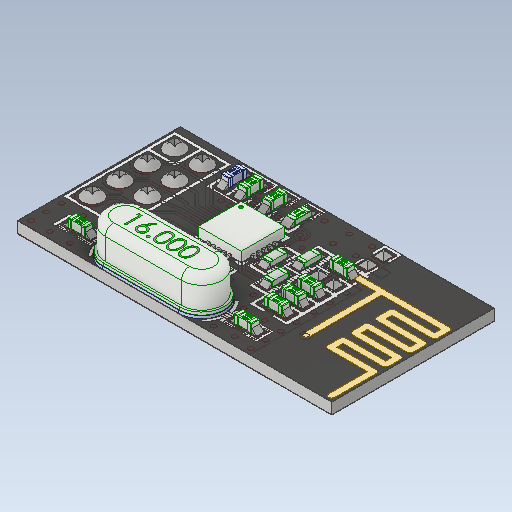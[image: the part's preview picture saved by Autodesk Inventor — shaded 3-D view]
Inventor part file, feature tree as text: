
AUTODESK INVENTOR PART (.ipt)
format: ipt  version: 2020.1 (Build 241239000, 239)  size: 6,878,208 bytes
history: mixed  units: mm
features: other x99, loft x29, boolean_combine x2, imported_body x1
ambient origin geometry x8: Origin, YZ Plane, XZ Plane, XY Plane, X Axis, Y Axis, Z Axis, Center Point
bodies: Solid1 (imported_parasolid), Solid2 (imported_parasolid), Solid3 (imported_parasolid), Solid4 (imported_parasolid), Solid5 (imported_parasolid), Solid6 (imported_parasolid), Solid7 (imported_parasolid), Solid8 (imported_parasolid), Solid9 (imported_parasolid), Solid10 (imported_parasolid), Solid11 (imported_parasolid), Solid12 (imported_parasolid), Solid13 (imported_parasolid), Solid14 (imported_parasolid), Solid15 (imported_parasolid), Solid16 (imported_parasolid), Solid17 (imported_parasolid), Solid18 (imported_parasolid), Solid19 (imported_parasolid), Solid20 (imported_parasolid), Solid21 (imported_parasolid), Solid22 (imported_parasolid), Solid23 (imported_parasolid), Solid24 (imported_parasolid), Solid25 (imported_parasolid), Solid26 (imported_parasolid), Solid27 (imported_parasolid), Solid28 (imported_parasolid), Solid29 (imported_parasolid), Solid30 (imported_parasolid), Solid31 (imported_parasolid), Solid32 (imported_parasolid), Solid33 (imported_parasolid), Solid34 (imported_parasolid), Solid35 (imported_parasolid), Solid36 (imported_parasolid), Solid37 (imported_parasolid), Solid38 (imported_parasolid), Solid39 (imported_parasolid), Solid40 (imported_parasolid), Solid41 (imported_parasolid), Solid42 (imported_parasolid), Solid43 (imported_parasolid), Solid44 (imported_parasolid), Solid45 (imported_parasolid), Solid46 (imported_parasolid), Solid47 (imported_parasolid), Solid48 (imported_parasolid), Solid49 (imported_parasolid), Solid50 (imported_parasolid), Solid51 (imported_parasolid), Solid52 (imported_parasolid), Solid53 (imported_parasolid), Solid54 (imported_parasolid), Solid55 (imported_parasolid), Solid56 (imported_parasolid), Solid57 (imported_parasolid), Solid58 (imported_parasolid), Solid59 (imported_parasolid), Solid60 (imported_parasolid), Solid61 (imported_parasolid), Solid62 (imported_parasolid), Solid63 (imported_parasolid), Solid64 (imported_parasolid), Solid65 (imported_parasolid), Solid66 (imported_parasolid), Solid67 (imported_parasolid), Solid68 (imported_parasolid), Solid69 (imported_parasolid), Solid70 (imported_parasolid), Solid71 (imported_parasolid), Solid72 (imported_parasolid), Solid73 (imported_parasolid), Solid74 (imported_parasolid), Solid75 (imported_parasolid), Solid76 (imported_parasolid), Solid77 (imported_parasolid), Solid78 (imported_parasolid), Solid79 (imported_parasolid), Solid80 (imported_parasolid), Solid81 (imported_parasolid), Solid82 (imported_parasolid), Solid83 (imported_parasolid), Solid84 (imported_parasolid), Solid85 (imported_parasolid), Solid86 (imported_parasolid), Solid87 (imported_parasolid), Solid88 (imported_parasolid), Solid89 (imported_parasolid), Solid90 (imported_parasolid), Solid91 (imported_parasolid), Solid92 (imported_parasolid), Solid93 (imported_parasolid), Solid94 (imported_parasolid), Solid95 (imported_parasolid), Solid96 (imported_parasolid), Solid97 (imported_parasolid), Solid98 (imported_parasolid), Solid99 (imported_parasolid), Solid100 (imported_parasolid), Solid101 (imported_parasolid), Solid102 (imported_parasolid), Solid103 (imported_parasolid), Solid104 (imported_parasolid), Solid105 (imported_parasolid), Solid106 (imported_parasolid), Solid107 (imported_parasolid), Solid108 (imported_parasolid), Solid109 (imported_parasolid), Solid110 (imported_parasolid), Solid111 (imported_parasolid), Solid112 (imported_parasolid), Solid113 (imported_parasolid), Solid114 (imported_parasolid), Solid115 (imported_parasolid), Solid116 (imported_parasolid), Solid117 (imported_parasolid), Solid118 (imported_parasolid), Solid119 (imported_parasolid), Solid120 (imported_parasolid), Solid121 (imported_parasolid), Solid122 (imported_parasolid), Solid123 (imported_parasolid), Solid124 (imported_parasolid), Solid125 (imported_parasolid), Solid126 (imported_parasolid), Solid127 (imported_parasolid), Solid128 (imported_parasolid), Solid129 (imported_parasolid), Solid130 (imported_parasolid)
feature tree (131):
  other  "PCB Body"
  other  "Cut-Extrude1[2]"
  other  "Cut-Extrude1[3]"
  other  "Cut-Extrude1[4]"
  other  "Cut-Extrude1[5]"
  other  "Cut-Extrude1[6]"
  other  "Cut-Extrude1[7]"
  other  "Cut-Extrude1[8]"
  other  "Cut-Extrude1[9]"
  other  "Cut-Extrude1[10]"
  other  "Cut-Extrude1[11]"
  other  "Cut-Extrude1[12]"
  other  "Cut-Extrude1[13]"
  other  "Cut-Extrude2[1]"
  other  "Cut-Extrude2[2]"
  other  "Cut-Extrude2[3]"
  other  "Cut-Extrude2[4]"
  other  "_Capacitor 1608_-_Solid7_"
  other  "Body-Move_Copy21"
  other  "Body-Move_Copy22"
  other  "_Resistor 1608_-_Imported1_"
  other  "Body-Move_Copy26"
  other  "Body-Move_Copy28"
  other  "Body-Move_Copy29[1]"
  other  "Body-Move_Copy29[2]"
  other  "Body-Move_Copy30"
  other  "Body-Move_Copy31"
  other  "Body-Move_Copy34"
  other  "_rg1608p-103-b_-_rg1608p-103-b_"
  other  "Body-Move_Copy38"
  other  "Body-Move_Copy39"
  other  "_QFN-20 with Pad_-_Вытянуть4_"
  other  "Boss-Extrude22"
  other  "Boss-Extrude28"
  other  "Body-Move_Copy50"
  other  "Boss-Extrude31"
  other  "Cut-Extrude3"
  loft  "Loft2"
  loft  "Loft4"
  loft  "Loft7"
  loft  "Loft9"
  loft  "Loft10"
  loft  "Loft12"
  loft  "Loft13"
  loft  "Loft14"
  loft  "Loft15"
  loft  "Loft16"
  loft  "Loft17"
  loft  "Loft18"
  loft  "Loft19"
  loft  "Loft20"
  loft  "Loft21"
  loft  "Loft22"
  loft  "Loft23"
  loft  "Loft24"
  loft  "Loft25"
  loft  "Loft26"
  loft  "Loft27"
  loft  "Loft28"
  loft  "Loft29"
  loft  "Loft30"
  loft  "Loft31"
  loft  "Loft32"
  loft  "Loft33"
  loft  "Loft34"
  loft  "Loft35"
  other  "Body-Move_Copy51[1]"
  other  "Body-Move_Copy51[2]"
  other  "Body-Move_Copy51[3]"
  other  "Body-Move_Copy51[4]"
  other  "Body-Move_Copy53[1]"
  other  "Body-Move_Copy53[2]"
  other  "Body-Move_Copy53[3]"
  other  "Body-Move_Copy53[4]"
  other  "Body-Move_Copy53[5]"
  other  "Body-Move_Copy57[1]"
  other  "Body-Move_Copy57[2]"
  other  "Body-Move_Copy57[3]"
  other  "Body-Move_Copy57[4]"
  other  "Body-Move_Copy57[5]"
  other  "Body-Move_Copy57[6]"
  other  "Body-Move_Copy57[7]"
  other  "Body-Move_Copy57[8]"
  other  "Body-Move_Copy57[9]"
  other  "Body-Move_Copy57[10]"
  other  "Boss-Extrude38[1]"
  other  "Boss-Extrude38[2]"
  other  "Boss-Extrude38[3]"
  other  "Boss-Extrude38[4]"
  other  "Cut-Extrude4[1]"
  other  "Cut-Extrude4[2]"
  other  "_Header 2_54 Vertical 1x2_-_Chamfer2_"
  other  "Cut-Extrude5[1]"
  other  "Cut-Extrude5[2]"
  other  "Cut-Extrude5[3]"
  other  "Cut-Extrude5[4]"
  other  "Cut-Extrude5[5]"
  other  "Cut-Extrude5[6]"
  other  "Cut-Extrude5[7]"
  other  "Cut-Extrude5[8]"
  other  "Boss-Extrude43"
  other  "Boss-Extrude45[1]"
  other  "Boss-Extrude45[2]"
  other  "Boss-Extrude45[3]"
  other  "Boss-Extrude45[4]"
  other  "Boss-Extrude45[5]"
  other  "Boss-Extrude45[6]"
  other  "Boss-Extrude45[7]"
  other  "Boss-Extrude45[8]"
  other  "Boss-Extrude45[9]"
  other  "Boss-Extrude45[10]"
  other  "Boss-Extrude45[11]"
  other  "Boss-Extrude45[12]"
  other  "Boss-Extrude45[13]"
  other  "Boss-Extrude45[14]"
  other  "Boss-Extrude45[15]"
  other  "Boss-Extrude45[16]"
  other  "Boss-Extrude45[17]"
  other  "Boss-Extrude45[18]"
  other  "Boss-Extrude45[19]"
  other  "Boss-Extrude45[20]"
  other  "Boss-Extrude45[21]"
  other  "Boss-Extrude45[22]"
  other  "Boss-Extrude45[23]"
  other  "Boss-Extrude45[24]"
  boolean_combine  "Combine15"
  boolean_combine  "Combine16"
  other  "LPattern2[1]"
  other  "LPattern2[2]"
  other  "LPattern2[3]"
  imported_body  NMx_Import_Brep_tag  [imported B-rep: ~522 faces, bbox_mm=None]
